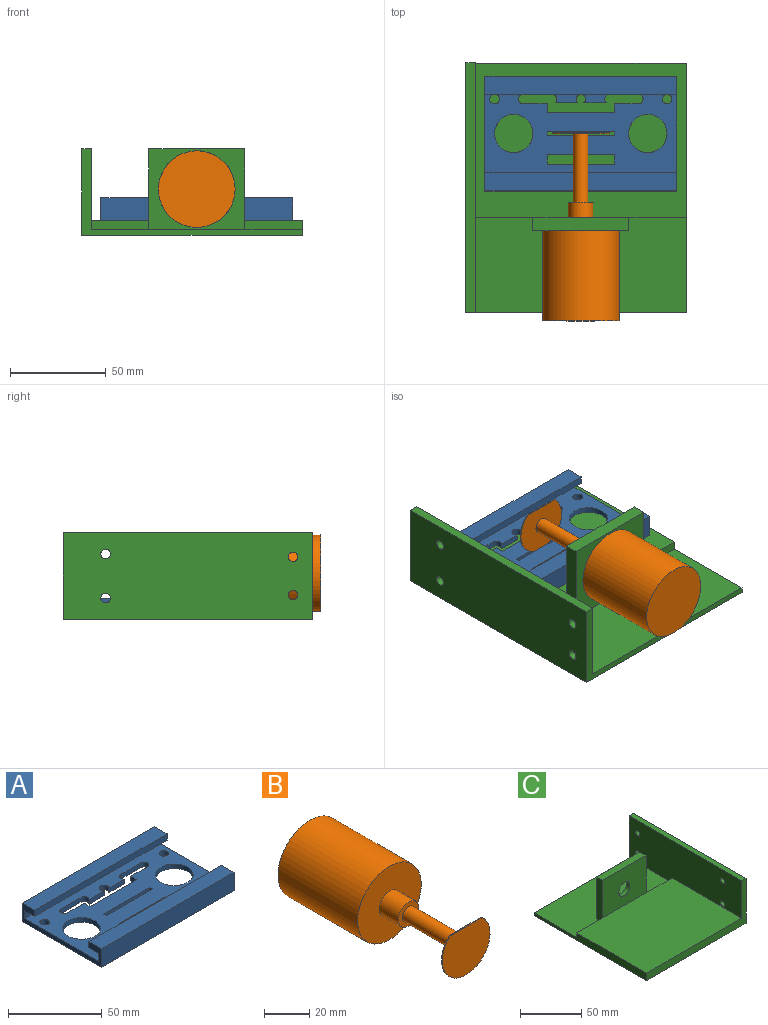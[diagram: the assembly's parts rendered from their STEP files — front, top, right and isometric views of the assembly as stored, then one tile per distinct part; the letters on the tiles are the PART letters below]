
ASSEMBLY  parts=3 mates=2
PART A: 40 faces, bbox 100x60x12 mm
  f0: plane 100x56mm, normal (0,0,1), area 4308.6mm2, adj f2,f3,f4,f5,f6,f7,f8,f13
  f1: plane 100x60mm, normal (0,0,-1), area 4708.6mm2, adj f2,f3,f4,f5,f6,f7,f14,f15
  f2: plane 11.86x3mm, normal (0,-1,0), area 35.6mm2, adj f0,f1,f31,f37
  f3: plane 11.86x3mm, normal (0,-1,0), area 35.6mm2, adj f0,f1,f36,f37
  f4: plane 3x2mm, normal (1,0,0), area 6mm2, adj f0,f1,f5,f7
  f5: plane 35x3mm, normal (0,1,0), area 105mm2, adj f0,f1,f4,f6
  f6: plane 3x2mm, normal (-1,0,0), area 6mm2, adj f0,f1,f5,f7
  f7: plane 35x3mm, normal (0,-1,0), area 105mm2, adj f0,f1,f4,f6
  f8: plane 100x5mm, normal (0,-1,0), area 500mm2, adj f0,f9,f24,f25
  f9: plane 100x7.5mm, normal (0,0,-1), area 750mm2, adj f8,f10,f24,f25
  f10: plane 100x4mm, normal (0,-1,0), area 400mm2, adj f9,f23,f24,f25
  f11: plane 100x4mm, normal (0,1,0), area 400mm2, adj f12,f24,f25,f28
  f12: plane 100x7.5mm, normal (0,0,-1), area 750mm2, adj f11,f13,f24,f25
  f13: plane 100x5mm, normal (0,1,0), area 500mm2, adj f0,f12,f24,f25
  f14: plane 35x3mm, normal (0,1,0), area 105mm2, adj f0,f1,f15,f17
  f15: plane 5x3mm, normal (-1,0,0), area 15mm2, adj f0,f1,f14,f16
  f16: plane 35x3mm, normal (0,-1,0), area 105mm2, adj f0,f1,f15,f17
  f17: plane 5x3mm, normal (1,0,0), area 15mm2, adj f0,f1,f14,f16
  f18: cylinder r=10mm len=20mm, axis (0,0,-1), area 188.5mm2, adj f0,f1
  f19: cylinder r=10mm len=20mm, axis (0,0,-1), area 188.5mm2, adj f0,f1
  f20: plane 4.45x3mm, normal (-1,0,0), area 13.3mm2, adj f0,f1,f22,f35
  f21: plane 4.45x3mm, normal (1,0,0), area 13.3mm2, adj f0,f1,f22,f32
  f22: plane 35x3mm, normal (0,1,0), area 105mm2, adj f0,f1,f20,f21
  f23: plane 100x9.5mm, normal (0,0,1), area 950mm2, adj f10,f24,f25,f27
  f24: plane 60x12mm, normal (-1,0,0), area 276mm2, adj f0,f1,f8,f9,f10,f11,f12,f13
  f25: plane 60x12mm, normal (1,0,0), area 276mm2, adj f0,f1,f8,f9,f10,f11,f12,f13
  f26: plane 100x12mm, normal (0,-1,0), area 1200mm2, adj f1,f24,f25,f28
  f27: plane 100x12mm, normal (0,1,0), area 1200mm2, adj f1,f23,f24,f25
  f28: plane 100x9.5mm, normal (0,0,1), area 950mm2, adj f11,f24,f25,f26
  f29: cylinder r=2.5mm len=5mm, axis (0,0,1), area 23.6mm2, adj f0,f1,f30,f32
  f30: plane 15x3mm, normal (0,-1,0), area 45mm2, adj f0,f1,f29,f31
  f31: cylinder r=2.5mm len=4.45mm, axis (0,0,1), area 18.5mm2, adj f0,f1,f2,f30
  f32: plane 12.5x3mm, normal (0,1,0), area 37.5mm2, adj f0,f1,f21,f29
  f33: cylinder r=2.5mm len=5mm, axis (0,0,1), area 23.6mm2, adj f0,f1,f34,f35
  f34: plane 15x3mm, normal (0,-1,0), area 45mm2, adj f0,f1,f33,f36
  f35: plane 12.5x3mm, normal (0,1,0), area 37.5mm2, adj f0,f1,f20,f33
  f36: cylinder r=2.5mm len=4.45mm, axis (0,0,1), area 18.5mm2, adj f0,f1,f3,f34
  f37: cylinder r=2.5mm len=5mm, axis (0,0,1), area 37mm2, adj f0,f1,f2,f3
  f38: cylinder r=2.5mm len=5mm, axis (0,0,1), area 47.1mm2, adj f0,f1
  f39: cylinder r=2.5mm len=5mm, axis (0,0,1), area 47.1mm2, adj f0,f1
PART B: 10 faces, bbox 40x98.2x40 mm
  f0: cylinder r=20mm len=50mm, axis (0,1,0), area 6283.2mm2, adj f1,f2
  f1: plane 40x40mm, normal (0,-1,0), area 1123.9mm2, adj f0,f3
  f2: plane 40x40mm, normal (0,1,0), area 1256.6mm2, adj f0
  f3: cylinder r=6.5mm len=13mm, axis (0,1,0), area 490.1mm2, adj f1,f4
  f4: plane 13x13mm, normal (0,-1,0), area 85mm2, adj f3,f5
  f5: cylinder r=3.9mm len=35.7mm, axis (0,1,0), area 874.3mm2, adj f4,f9
  f6: plane 20x0.5mm, normal (0,0,1), area 10mm2, adj f7,f8,f9
  f7: cylinder r=15mm len=30mm, axis (0,1,0), area 36.2mm2, adj f6,f8,f9
  f8: plane 30x26.18mm, normal (0,-1,0), area 654.5mm2, adj f6,f7
  f9: plane 30x26.18mm, normal (0,1,0), area 606.7mm2, adj f5,f6,f7
PART C: 22 faces, bbox 115x130x45 mm
  f0: cylinder r=6.5mm len=13mm, axis (0,-1,0), area 163.4mm2, adj f8,f12
  f1: plane 110x49.51mm, normal (0,0,1), area 5095.8mm2, adj f2,f3,f6,f7,f8,f9,f14,f15
  f2: plane 115x45mm, normal (0,1,0), area 555mm2, adj f1,f3,f5,f15,f16,f21
  f3: plane 130x7.5mm, normal (-1,0,0), area 752.2mm2, adj f1,f2,f4,f5,f13,f14
  f4: plane 115x45mm, normal (0,-1,0), area 1050mm2, adj f3,f5,f13,f15,f16,f21
  f5: plane 130x115mm, normal (0,0,-1), area 14950mm2, adj f2,f3,f4,f21
  f6: plane 50x42mm, normal (0,1,0), area 843.4mm2, adj f1,f7,f9,f10,f11
  f7: plane 42x7mm, normal (-1,0,0), area 294mm2, adj f1,f6,f8,f10
  f8: plane 50x42mm, normal (0,-1,0), area 1967.3mm2, adj f0,f1,f7,f9,f10
  f9: plane 42x7mm, normal (1,0,0), area 294mm2, adj f1,f6,f8,f10
  f10: plane 50x7mm, normal (0,0,1), area 350mm2, adj f6,f7,f8,f9
  f11: cylinder r=20mm len=40mm, axis (0,1,0), area 377mm2, adj f6,f12
  f12: plane 40x40mm, normal (0,1,0), area 1123.9mm2, adj f0,f11
  f13: plane 110x80.49mm, normal (0,0,1), area 8854.2mm2, adj f3,f4,f14,f15
  f14: plane 110x4.5mm, normal (0,1,0), area 495mm2, adj f1,f3,f13,f15
  f15: plane 130x42mm, normal (-1,0,0), area 5019.2mm2, adj f1,f2,f4,f13,f14,f16,f17,f18
  f16: plane 130x5mm, normal (0,0,1), area 650mm2, adj f2,f4,f15,f21
  f17: cylinder r=2.5mm len=5mm, axis (-1,0,0), area 78.5mm2, adj f15,f21
  f18: cylinder r=2.5mm len=5mm, axis (-1,0,0), area 78.5mm2, adj f15,f21
  f19: cylinder r=2.5mm len=5mm, axis (-1,0,0), area 78.5mm2, adj f15,f21
  f20: cylinder r=2.5mm len=5mm, axis (-1,0,0), area 78.5mm2, adj f15,f21
  f21: plane 130x45mm, normal (1,0,0), area 5771.5mm2, adj f2,f4,f5,f16,f17,f18,f19,f20
PLACE A t=(27.15,102.24,21.06)mm
PLACE B rot(axis=(0,0,1),180deg) t=(-60.7,-30.57,8.18)mm
PLACE C rot(axis=(0,0,-1),180deg) t=(192.45,38.99,18.56)mm
MATE revolute B.f0 <-> C.f0  axis (0,1,0) through (192.45,19.43,42.56)mm
MATE fastened C.f13 <-> A.f1  axis (0,0,1) through (192.45,63.74,26.06)mm
